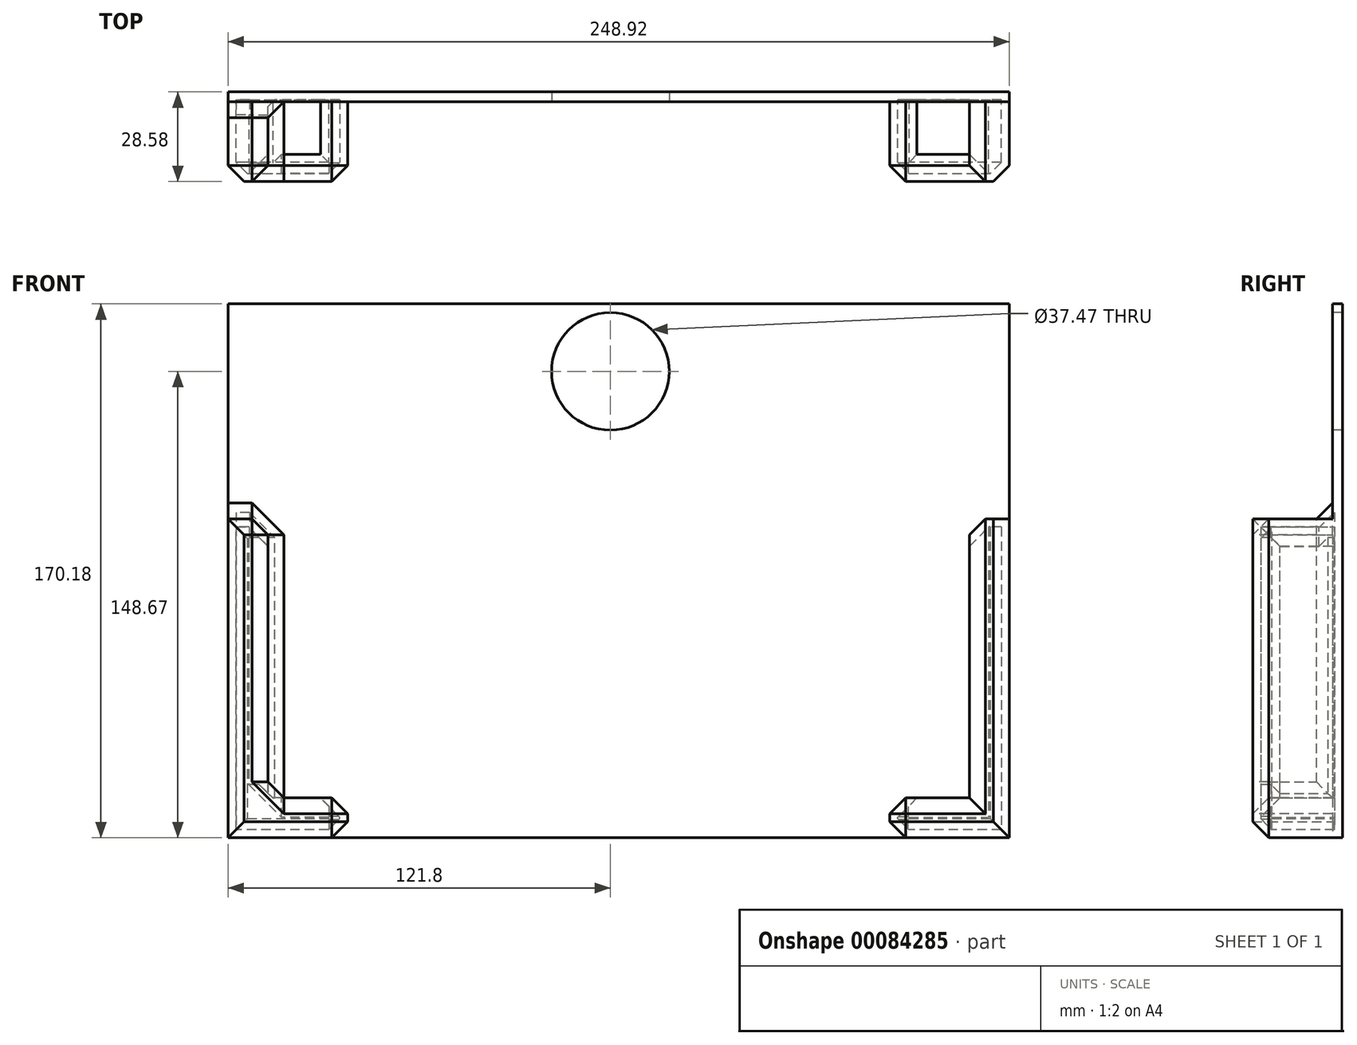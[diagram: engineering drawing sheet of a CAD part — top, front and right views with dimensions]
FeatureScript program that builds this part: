
annotation { "Feature Type Name" : "Feature", "Feature Type Description" : "" }
export const myFeature = defineFeature(function(context is Context, id is Id, definition is map)
    precondition{}
    {
        {
            var Q0;
            Q0=qCreatedBy(makeId("Front.planeOp"),FACE);
            var sketch = newSketch(context, id + "F0", { "sketchPlane" : qUnion([Q0])});
            skLineSegment(sketch, "E0.bottom", {"start": v(-121.8, 21.51) * mm, "end": v(127.12, 21.51) * mm});
            skLineSegment(sketch, "E0.top", {"start": v(-121.8, -148.67) * mm, "end": v(127.12, -148.67) * mm});
            skLineSegment(sketch, "E0.left", {"start": v(-121.8, 21.51) * mm, "end": v(-121.8, -148.67) * mm});
            skLineSegment(sketch, "E0.right", {"start": v(127.12, 21.51) * mm, "end": v(127.12, -148.67) * mm});
            skLineSegment(sketch, "E1.bottom", {"start": v(-161.7, 242.5) * mm, "end": v(-124.3, 242.5) * mm, "construction": true});
            skLineSegment(sketch, "E1.top", {"start": v(-161.7, 203.36) * mm, "end": v(-124.3, 203.36) * mm, "construction": true});
            skLineSegment(sketch, "E1.left", {"start": v(-161.7, 242.5) * mm, "end": v(-161.7, 203.36) * mm, "construction": true});
            skLineSegment(sketch, "E1.right", {"start": v(-124.3, 242.5) * mm, "end": v(-124.3, 203.36) * mm, "construction": true});
            skLineSegment(sketch, "E2.bottom", {"start": v(-112.8, -154.93) * mm, "end": v(-115.42, -154.93) * mm});
            skLineSegment(sketch, "E2.top", {"start": v(-112.8, -154.74) * mm, "end": v(-115.42, -154.74) * mm});
            skLineSegment(sketch, "E2.left", {"start": v(-112.8, -154.93) * mm, "end": v(-112.8, -154.74) * mm});
            skLineSegment(sketch, "E2.right", {"start": v(-115.42, -154.93) * mm, "end": v(-115.42, -154.74) * mm});
            skSolve(sketch);
        }
        {
            var Q0;
            Q0=makeQuery(id+"F0.imprint","IMPRINT",FACE,{"disambiguationData":[TD([[makeQuery(id+"F0.imprint","IMPRINT",EDGE,{"derivedFrom":sQuery(id+"F0.wireOp",EDGE,"E0.bottom")}),-1.0]])]});
            extrude(context, id + "F1", {"entities" : qUnion([Q0]), "depth" : 3.17 * mm});
        }
        {
            var Q0;
            Q0=makeQuery(id+"F1.opExtrude","CAP_FACE",FACE,{"disambiguationData":[OSD([sQuery(id+"F0.wireOp",EDGE,"E0.bottom"),sQuery(id+"F0.wireOp",EDGE,"E0.top"),sQuery(id+"F0.wireOp",EDGE,"E0.left"),sQuery(id+"F0.wireOp",EDGE,"E0.right")])],"isStart":false});
            var sketch = newSketch(context, id + "F2", { "sketchPlane" : qUnion([Q0])});
            skLineSegment(sketch, "E3.bottom", {"start": v(-121.8, -47.07) * mm, "end": v(-109.1, -47.07) * mm});
            skLineSegment(sketch, "E3.top", {"start": v(-121.8, -148.67) * mm, "end": v(-109.1, -148.67) * mm});
            skLineSegment(sketch, "E3.left", {"start": v(-121.8, -47.07) * mm, "end": v(-121.8, -148.67) * mm});
            skLineSegment(sketch, "E3.right", {"start": v(-109.1, -47.07) * mm, "end": v(-109.1, -148.67) * mm});
            skLineSegment(sketch, "E4.bottom", {"start": v(127.12, -47.07) * mm, "end": v(114.42, -47.07) * mm});
            skLineSegment(sketch, "E4.top", {"start": v(127.12, -148.67) * mm, "end": v(114.42, -148.67) * mm});
            skLineSegment(sketch, "E4.left", {"start": v(127.12, -47.07) * mm, "end": v(127.12, -148.67) * mm});
            skLineSegment(sketch, "E4.right", {"start": v(114.42, -47.07) * mm, "end": v(114.42, -148.67) * mm});
            skLineSegment(sketch, "E5.bottom", {"start": v(-83.7, -135.97) * mm, "end": v(-109.1, -135.97) * mm});
            skLineSegment(sketch, "E5.top", {"start": v(-83.7, -148.67) * mm, "end": v(-109.1, -148.67) * mm});
            skLineSegment(sketch, "E5.left", {"start": v(-83.7, -135.97) * mm, "end": v(-83.7, -148.67) * mm});
            skLineSegment(sketch, "E5.right", {"start": v(-109.1, -135.97) * mm, "end": v(-109.1, -148.67) * mm});
            skLineSegment(sketch, "E6.bottom", {"start": v(89.02, -135.97) * mm, "end": v(114.42, -135.97) * mm});
            skLineSegment(sketch, "E6.top", {"start": v(89.02, -148.67) * mm, "end": v(114.42, -148.67) * mm});
            skLineSegment(sketch, "E6.left", {"start": v(89.02, -135.97) * mm, "end": v(89.02, -148.67) * mm});
            skLineSegment(sketch, "E6.right", {"start": v(114.42, -135.97) * mm, "end": v(114.42, -148.67) * mm});
            skSolve(sketch);
        }
        {
            var Q0;
            Q0=makeQuery(id+"F2.imprint","IMPRINT",FACE,{"disambiguationData":[TD([[makeQuery(id+"F2.imprint","IMPRINT",EDGE,{"derivedFrom":sQuery(id+"F2.wireOp",EDGE,"E5.bottom")}),1.0]])]});
            var Q1;
            Q1=makeQuery(id+"F2.imprint","IMPRINT",FACE,{"disambiguationData":[TD([[makeQuery(id+"F2.imprint","IMPRINT",EDGE,{"derivedFrom":sQuery(id+"F2.wireOp",EDGE,"E6.bottom")}),-1.0]])]});
            var Q2;
            Q2=makeQuery(id+"F2.imprint","IMPRINT",FACE,{"disambiguationData":[TD([[makeQuery(id+"F2.imprint","IMPRINT",EDGE,{"derivedFrom":sQuery(id+"F2.wireOp",EDGE,"E3.bottom")}),-1.0]])]});
            var Q3;
            Q3=makeQuery(id+"F2.imprint","IMPRINT",FACE,{"disambiguationData":[TD([[makeQuery(id+"F2.imprint","IMPRINT",EDGE,{"derivedFrom":sQuery(id+"F2.wireOp",EDGE,"E4.bottom")}),1.0]])]});
            extrude(context, id + "F3", {"entities" : qUnion([Q0, Q1, Q2, Q3]), "operationType" : NewBodyOperationType.ADD, "depth" : 25.4 * mm});
        }
        {
            var Q0;
            Q0=makeQuery(id+"F3.opExtrude","SWEPT_EDGE",EDGE,{"disambiguationData":[OSD([sQuery(id+"F0.wireOp",EDGE,"E0.top"),sQuery(id+"F2.wireOp",EDGE,"E6.top"),sQuery(id+"F2.wireOp",EDGE,"E6.left")])]});
            var Q1;
            Q1=makeQuery(id+"F3.opExtrude","SWEPT_EDGE",EDGE,{"disambiguationData":[OSD([sQuery(id+"F2.wireOp",EDGE,"E6.bottom"),sQuery(id+"F2.wireOp",EDGE,"E6.left")])]});
            var Q2;
            Q2=makeQuery(id+"F3.opExtrude","CAP_EDGE",EDGE,{"disambiguationData":[OSD([sQuery(id+"F2.wireOp",EDGE,"E6.left")])],"isStart":false});
            var Q3;
            Q3=makeQuery(id+"F3.opExtrude","CAP_EDGE",EDGE,{"disambiguationData":[OSD([sQuery(id+"F2.wireOp",EDGE,"E4.top"),sQuery(id+"F2.wireOp",EDGE,"E6.top")])],"isStart":false});
            var Q4;
            Q4=makeQuery(id+"F3.opExtrude","CAP_EDGE",EDGE,{"disambiguationData":[OSD([sQuery(id+"F2.wireOp",EDGE,"E6.bottom")])],"isStart":false});
            var Q5;
            Q5=makeQuery(id+"F3.opExtrude","CAP_EDGE",EDGE,{"disambiguationData":[OSD([sQuery(id+"F2.wireOp",EDGE,"E4.right")])],"isStart":false});
            var Q6;
            Q6=makeQuery(id+"F3.opExtrude","CAP_EDGE",EDGE,{"disambiguationData":[OSD([sQuery(id+"F2.wireOp",EDGE,"E4.left")])],"isStart":false});
            var Q7;
            Q7=makeQuery(id+"F3.opExtrude","CAP_EDGE",EDGE,{"disambiguationData":[OSD([sQuery(id+"F2.wireOp",EDGE,"E4.right")])],"isStart":true});
            var Q8;
            Q8=makeQuery(id+"F3.opExtrude","CAP_EDGE",EDGE,{"disambiguationData":[OSD([sQuery(id+"F2.wireOp",EDGE,"E3.top"),sQuery(id+"F2.wireOp",EDGE,"E5.top")])],"isStart":false});
            var Q9;
            Q9=makeQuery(id+"F3.opExtrude","SWEPT_EDGE",EDGE,{"disambiguationData":[OSD([sQuery(id+"F0.wireOp",EDGE,"E0.top"),sQuery(id+"F2.wireOp",EDGE,"E5.top"),sQuery(id+"F2.wireOp",EDGE,"E5.left")])]});
            var Q10;
            Q10=makeQuery(id+"F3.opExtrude","SWEPT_EDGE",EDGE,{"disambiguationData":[OSD([sQuery(id+"F2.wireOp",EDGE,"E5.bottom"),sQuery(id+"F2.wireOp",EDGE,"E5.left")])]});
            var Q11;
            Q11=makeQuery(id+"F3.opExtrude","CAP_EDGE",EDGE,{"disambiguationData":[OSD([sQuery(id+"F2.wireOp",EDGE,"E5.left")])],"isStart":false});
            var Q12;
            Q12=makeQuery(id+"F3.opExtrude","CAP_EDGE",EDGE,{"disambiguationData":[OSD([sQuery(id+"F2.wireOp",EDGE,"E5.bottom")])],"isStart":false});
            var Q13;
            Q13=makeQuery(id+"F3.opExtrude","CAP_EDGE",EDGE,{"disambiguationData":[OSD([sQuery(id+"F2.wireOp",EDGE,"E3.left")])],"isStart":false});
            var Q14;
            Q14=makeQuery(id+"F3.opExtrude","CAP_EDGE",EDGE,{"disambiguationData":[OSD([sQuery(id+"F2.wireOp",EDGE,"E3.right")])],"isStart":false});
            var Q15;
            Q15=makeQuery(id+"F3.opExtrude","CAP_EDGE",EDGE,{"disambiguationData":[OSD([sQuery(id+"F2.wireOp",EDGE,"E3.right")])],"isStart":true});
            var Q16;
            Q16=makeQuery(id+"F3.opExtrude","SWEPT_FACE",FACE,{"disambiguationData":[OSD([sQuery(id+"F2.wireOp",EDGE,"E3.right")])]});
            var Q17;
            Q17=makeQuery(id+"F3.opExtrude","CAP_EDGE",EDGE,{"disambiguationData":[OSD([sQuery(id+"F2.wireOp",EDGE,"E3.bottom")])],"isStart":false});
            var Q18;
            Q18=makeQuery(id+"F3.opExtrude","SWEPT_EDGE",EDGE,{"disambiguationData":[OSD([sQuery(id+"F2.wireOp",EDGE,"E4.bottom"),sQuery(id+"F2.wireOp",EDGE,"E4.right")])]});
            var Q19;
            Q19=makeQuery(id+"F3.opExtrude","CAP_EDGE",EDGE,{"disambiguationData":[OSD([sQuery(id+"F2.wireOp",EDGE,"E4.bottom")])],"isStart":true});
            var Q20;
            Q20=makeQuery(id+"F3.opExtrude","CAP_EDGE",EDGE,{"disambiguationData":[OSD([sQuery(id+"F2.wireOp",EDGE,"E3.bottom")])],"isStart":true});
            chamfer(context, id + "F4", {"entities" : qUnion([Q0, Q1, Q2, Q3, Q4, Q5, Q6, Q7, Q8, Q9, Q10, Q11, Q12, Q13, Q14, Q15, Q16, Q17, Q18, Q19, Q20]), "width" : 5.08 * mm, "tangentPropagation" : true});
        }
        {
            var Q0;
            Q0=makeQuery(id+"F3.opExtrude","SWEPT_FACE",FACE,{"disambiguationData":[OSD([sQuery(id+"F2.wireOp",EDGE,"E3.right")])]});
            var Q1;
            Q1=makeQuery(id+"F3.opExtrude","SWEPT_FACE",FACE,{"disambiguationData":[OSD([sQuery(id+"F2.wireOp",EDGE,"E5.bottom")])]});
            var Q2;
            Q2=makeQuery(id+"F3.opExtrude","SWEPT_FACE",FACE,{"disambiguationData":[OSD([sQuery(id+"F2.wireOp",EDGE,"E4.right")])]});
            var Q3;
            Q3=makeQuery(id+"F3.opExtrude","SWEPT_FACE",FACE,{"disambiguationData":[OSD([sQuery(id+"F2.wireOp",EDGE,"E6.bottom")])]});
            shell(context, id + "F5", {"entities" : qUnion([Q0, Q1, Q2, Q3]), "thickness" : 2.54 * mm});
        }
        {
            var Q0;
            Q0=makeQuery(id+"F1.opExtrude","CAP_FACE",FACE,{"disambiguationData":[OSD([sQuery(id+"F0.wireOp",EDGE,"E0.bottom"),sQuery(id+"F0.wireOp",EDGE,"E0.top"),sQuery(id+"F0.wireOp",EDGE,"E0.left"),sQuery(id+"F0.wireOp",EDGE,"E0.right")])],"isStart":false});
            var sketch = newSketch(context, id + "F6", { "sketchPlane" : qUnion([Q0])});
            skCircle(sketch, "E7", {"center": v(0, 0) * mm, "radius": 18.74 * mm});
            skSolve(sketch);
        }
        {
            var Q0;
            Q0=makeQuery(id+"F6.imprint","IMPRINT",FACE,{"disambiguationData":[TD([[makeQuery(id+"F6.imprint","IMPRINT",EDGE,{"derivedFrom":sQuery(id+"F6.wireOp",EDGE,"E7")}),1.0]])]});
            extrude(context, id + "F7", {"entities" : qUnion([Q0]), "operationType" : NewBodyOperationType.REMOVE, "oppositeDirection" : true, "depth" : 25.4 * mm});
        }
    });
